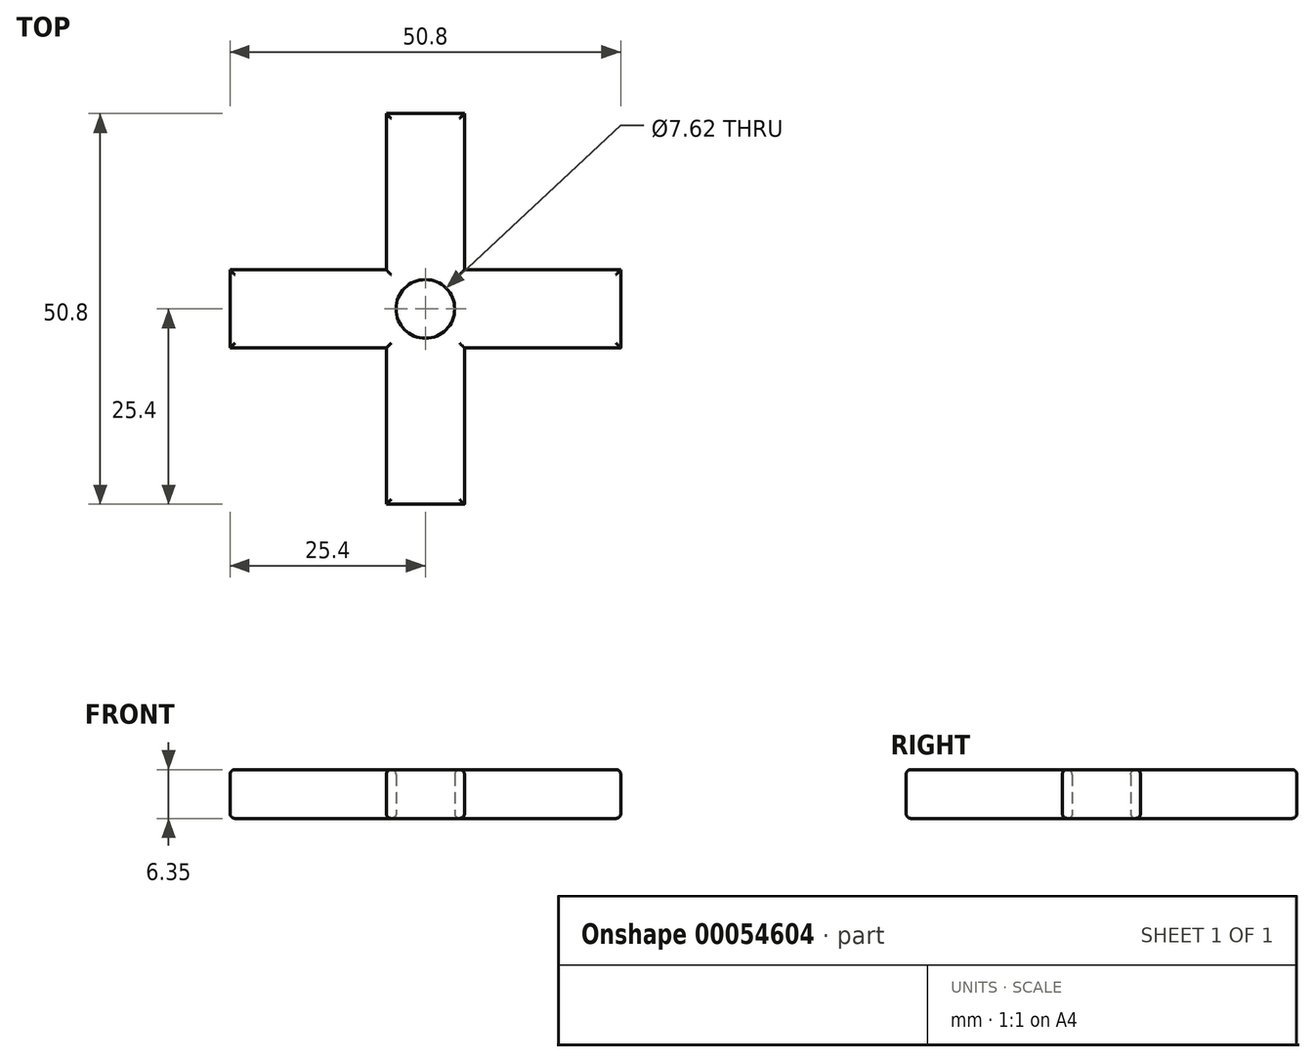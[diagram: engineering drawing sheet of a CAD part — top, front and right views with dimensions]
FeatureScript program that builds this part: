
annotation { "Feature Type Name" : "Feature", "Feature Type Description" : "" }
export const myFeature = defineFeature(function(context is Context, id is Id, definition is map)
    precondition{}
    {
        {
            var Q0;
            Q0=qCreatedBy(makeId("Top.planeOp"),FACE);
            var sketch = newSketch(context, id + "F0", { "sketchPlane" : qUnion([Q0])});
            skCircle(sketch, "E0", {"center": v(0, 0) * mm, "radius": 3.81 * mm});
            skCircle(sketch, "E1", {"center": v(0, 0) * mm, "radius": 6.35 * mm});
            skSolve(sketch);
        }
        {
            var Q0;
            Q0=qSketchRegion(id+"F0",true);
            extrude(context, id + "F1", {"entities" : qUnion([Q0]), "depth" : 6.35 * mm});
        }
        {
            var Q0;
            Q0=makeQuery(id+"F1.opExtrude","CAP_FACE",FACE,{"disambiguationData":[OSD([sQuery(id+"F0.wireOp",EDGE,"E0"),sQuery(id+"F0.wireOp",EDGE,"E1")])],"isStart":false});
            var sketch = newSketch(context, id + "F2", { "sketchPlane" : qUnion([Q0])});
            skLineSegment(sketch, "E2", {"start": v(25.4, 5.08) * mm, "end": v(25.4, -5.08) * mm});
            skLineSegment(sketch, "E3", {"start": v(-25.4, 5.08) * mm, "end": v(-25.4, -5.08) * mm});
            skPoint(sketch, "E3.startSnap0", {"position": v(-25.4, 5.27) * mm});
            skLineSegment(sketch, "E4", {"start": v(-5.08, -25.4) * mm, "end": v(5.08, -25.4) * mm});
            skLineSegment(sketch, "E5", {"start": v(5.08, 25.4) * mm, "end": v(-5.08, 25.4) * mm});
            skLineSegment(sketch, "E6", {"start": v(-25.4, 5.08) * mm, "end": v(-3.81, 5.08) * mm});
            skLineSegment(sketch, "E7", {"start": v(-25.4, -5.08) * mm, "end": v(-3.8, -5.08) * mm});
            skLineSegment(sketch, "E8", {"start": v(-3.8, -5.08) * mm, "end": v(-3.81, 5.08) * mm});
            skLineSegment(sketch, "E9", {"start": v(-5.08, 25.4) * mm, "end": v(-5.08, 3.8) * mm});
            skLineSegment(sketch, "E10", {"start": v(-5.08, 3.8) * mm, "end": v(5.08, 3.8) * mm});
            skLineSegment(sketch, "E11", {"start": v(5.08, 3.8) * mm, "end": v(5.08, 25.4) * mm});
            skLineSegment(sketch, "E12", {"start": v(25.4, 5.08) * mm, "end": v(3.8, 5.08) * mm});
            skLineSegment(sketch, "E13", {"start": v(3.8, 5.08) * mm, "end": v(3.81, -5.08) * mm});
            skLineSegment(sketch, "E14", {"start": v(3.8, -5.08) * mm, "end": v(25.4, -5.08) * mm});
            skLineSegment(sketch, "E15", {"start": v(5.08, -25.4) * mm, "end": v(5.08, -3.8) * mm});
            skLineSegment(sketch, "E16", {"start": v(5.08, -3.8) * mm, "end": v(-5.08, -3.8) * mm});
            skLineSegment(sketch, "E17", {"start": v(-5.08, -3.8) * mm, "end": v(-5.08, -25.4) * mm});
            skSolve(sketch);
        }
        {
            var Q0;
            Q0=qSketchRegion(id+"F2",true);
            extrude(context, id + "F3", {"entities" : qUnion([Q0]), "operationType" : NewBodyOperationType.ADD, "oppositeDirection" : true, "depth" : 6.35 * mm});
        }
        {
            var Q0;
            Q0=makeQuery(id+"F1.opExtrude","CAP_EDGE",EDGE,{"disambiguationData":[OSD([sQuery(id+"F0.wireOp",EDGE,"E0")])],"isStart":false});
            var Q1;
            Q1=makeQuery(id+"F1.opExtrude","CAP_EDGE",EDGE,{"disambiguationData":[OSD([sQuery(id+"F0.wireOp",EDGE,"E0")])],"isStart":true});
            var Q2;
            Q2=makeQuery(id+"F3.boolean.opBoolean","MERGE",FACE,{"derivedFrom":[makeQuery(id+"F1.opExtrude","CAP_FACE",FACE,{"disambiguationData":[OSD([sQuery(id+"F0.wireOp",EDGE,"E0"),sQuery(id+"F0.wireOp",EDGE,"E1")])],"isStart":true}),makeQuery(id+"F3.opExtrude","CAP_FACE",FACE,{"disambiguationData":[OSD([sQuery(id+"F2.wireOp",EDGE,"E2"),sQuery(id+"F2.wireOp",EDGE,"E3"),sQuery(id+"F2.wireOp",EDGE,"E4"),sQuery(id+"F2.wireOp",EDGE,"E5"),sQuery(id+"F2.wireOp",EDGE,"E6"),sQuery(id+"F2.wireOp",EDGE,"E7"),sQuery(id+"F2.wireOp",EDGE,"E8"),sQuery(id+"F2.wireOp",EDGE,"E9"),sQuery(id+"F2.wireOp",EDGE,"E10"),sQuery(id+"F2.wireOp",EDGE,"E11"),sQuery(id+"F2.wireOp",EDGE,"E12"),sQuery(id+"F2.wireOp",EDGE,"E13"),sQuery(id+"F2.wireOp",EDGE,"E14"),sQuery(id+"F2.wireOp",EDGE,"E15"),sQuery(id+"F2.wireOp",EDGE,"E16"),sQuery(id+"F2.wireOp",EDGE,"E17")])],"isStart":false})]});
            var Q3;
            Q3=makeQuery(id+"F3.boolean.opBoolean","MERGE",FACE,{"derivedFrom":[makeQuery(id+"F1.opExtrude","CAP_FACE",FACE,{"disambiguationData":[OSD([sQuery(id+"F0.wireOp",EDGE,"E0"),sQuery(id+"F0.wireOp",EDGE,"E1")])],"isStart":false}),makeQuery(id+"F3.opExtrude","CAP_FACE",FACE,{"disambiguationData":[OSD([sQuery(id+"F2.wireOp",EDGE,"E2"),sQuery(id+"F2.wireOp",EDGE,"E3"),sQuery(id+"F2.wireOp",EDGE,"E4"),sQuery(id+"F2.wireOp",EDGE,"E5"),sQuery(id+"F2.wireOp",EDGE,"E6"),sQuery(id+"F2.wireOp",EDGE,"E7"),sQuery(id+"F2.wireOp",EDGE,"E8"),sQuery(id+"F2.wireOp",EDGE,"E9"),sQuery(id+"F2.wireOp",EDGE,"E10"),sQuery(id+"F2.wireOp",EDGE,"E11"),sQuery(id+"F2.wireOp",EDGE,"E12"),sQuery(id+"F2.wireOp",EDGE,"E13"),sQuery(id+"F2.wireOp",EDGE,"E14"),sQuery(id+"F2.wireOp",EDGE,"E15"),sQuery(id+"F2.wireOp",EDGE,"E16"),sQuery(id+"F2.wireOp",EDGE,"E17")])],"isStart":true})]});
            fillet(context, id + "F4", {"entities" : qUnion([Q0, Q1, Q2, Q3]), "radius" : 0.64 * mm, "tangentPropagation" : true, "allowEdgeOverflow" : false});
        }
    });
